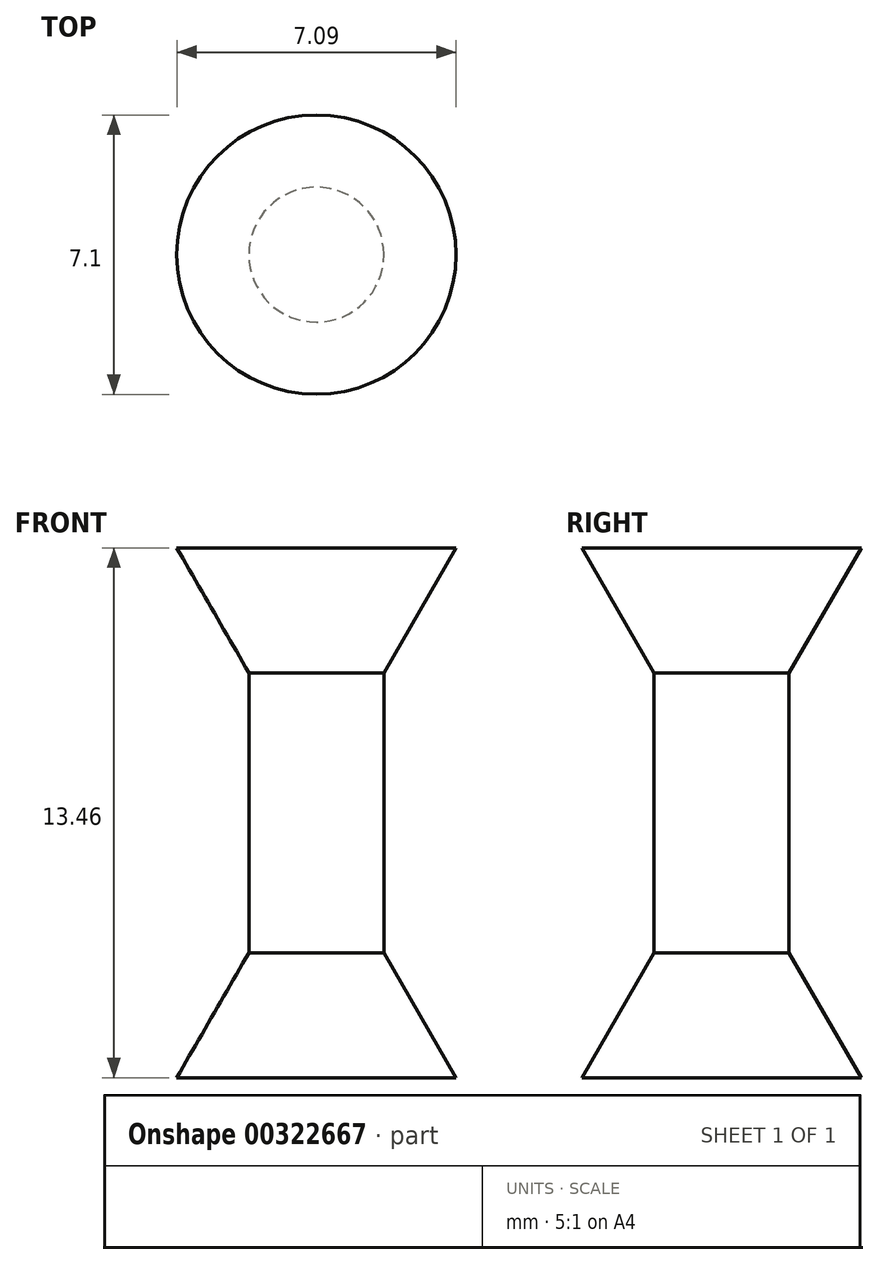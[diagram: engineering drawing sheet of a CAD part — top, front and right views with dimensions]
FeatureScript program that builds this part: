
annotation { "Feature Type Name" : "Feature", "Feature Type Description" : "" }
export const myFeature = defineFeature(function(context is Context, id is Id, definition is map)
    precondition{}
    {
        {
            var Q0;
            Q0=qCreatedBy(makeId("Front.planeOp"),FACE);
            var sketch = newSketch(context, id + "F0", { "sketchPlane" : qUnion([Q0])});
            skLineSegment(sketch, "E0", {"start": v(0, 5.63) * mm, "end": v(0, -1.49) * mm});
            skLineSegment(sketch, "E1", {"start": v(0, -1.49) * mm, "end": v(-1.83, -4.66) * mm});
            skLineSegment(sketch, "E2", {"start": v(-1.83, -4.66) * mm, "end": v(1.71, -4.66) * mm});
            skLineSegment(sketch, "E3", {"start": v(1.71, -4.66) * mm, "end": v(1.71, 8.8) * mm});
            skLineSegment(sketch, "E4", {"start": v(1.71, 8.8) * mm, "end": v(-1.83, 8.8) * mm});
            skLineSegment(sketch, "E5", {"start": v(-1.83, 8.8) * mm, "end": v(0, 5.63) * mm});
            skSolve(sketch);
        }
        {
            var Q0;
            Q0=makeQuery(id+"F0.imprint","IMPRINT",FACE,{"disambiguationData":[TD([[makeQuery(id+"F0.imprint","IMPRINT",EDGE,{"derivedFrom":sQuery(id+"F0.wireOp",EDGE,"E0")}),1.0]])]});
            var Q1;
            Q1=sQuery(id+"F0.wireOp",EDGE,"E3");
            revolve(context, id + "F1", {"entities" : qUnion([Q0]), "axis" : qUnion([Q1]), "revolveType" : RevolveType.FULL});
        }
    });
